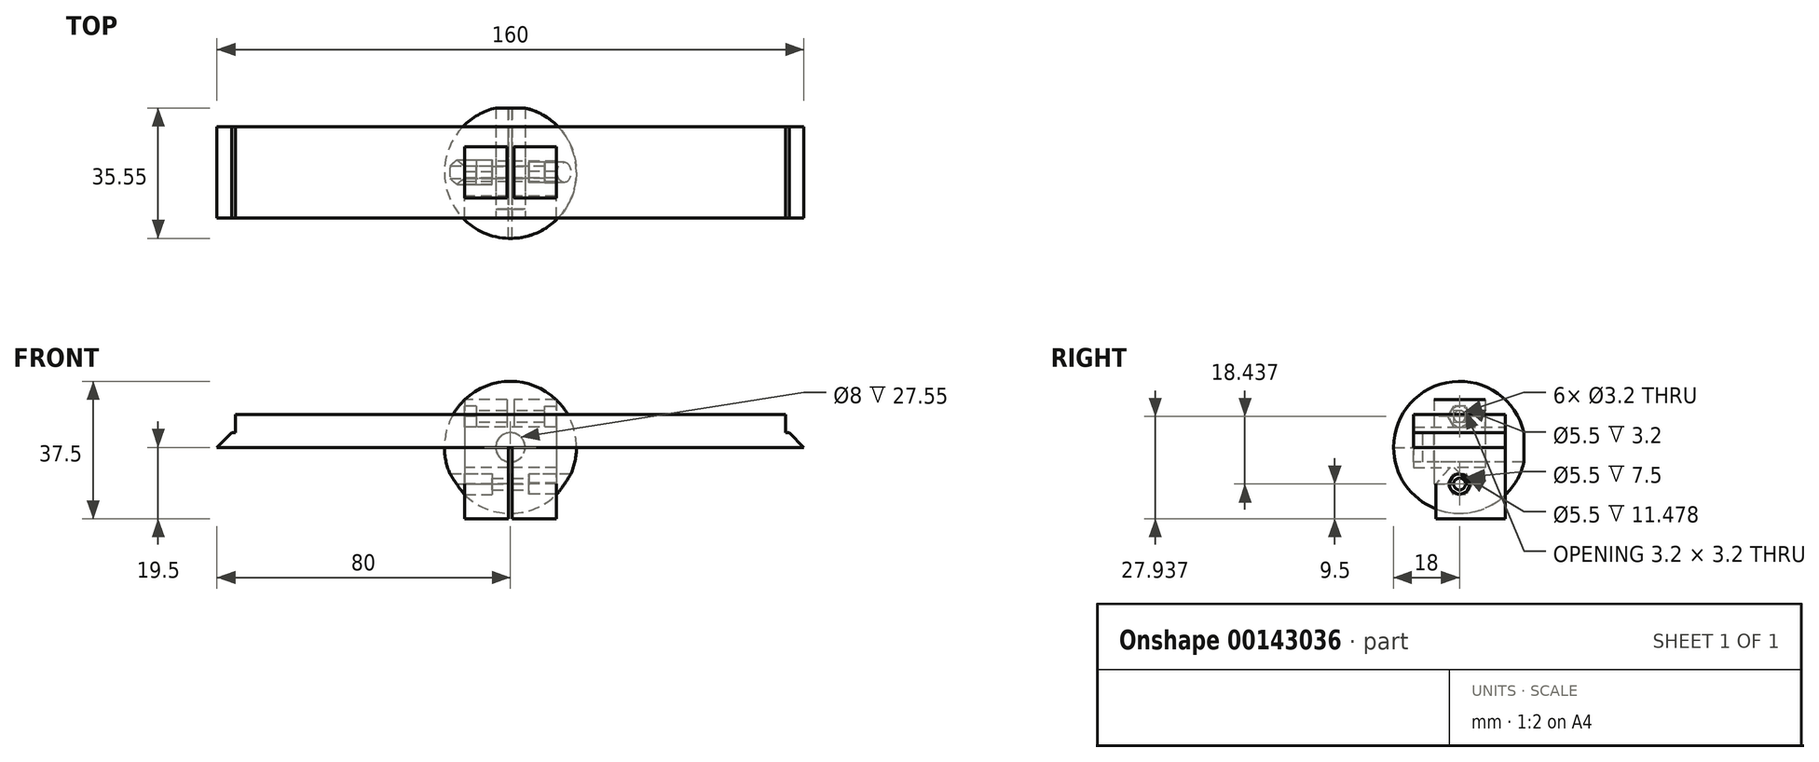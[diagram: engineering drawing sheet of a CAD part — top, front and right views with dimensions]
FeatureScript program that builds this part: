
annotation { "Feature Type Name" : "Feature", "Feature Type Description" : "" }
export const myFeature = defineFeature(function(context is Context, id is Id, definition is map)
    precondition{}
    {
        {
            var Q0;
            Q0=qCreatedBy(makeId("Right.planeOp"),FACE);
            var sketch = newSketch(context, id + "F0", { "sketchPlane" : qUnion([Q0])});
            skLineSegment(sketch, "E0.bottom", {"start": v(-7, 13) * mm, "end": v(7, 13) * mm});
            skLineSegment(sketch, "E0.top", {"start": v(-7, -10) * mm, "end": v(3, -10) * mm});
            skLineSegment(sketch, "E0.left", {"start": v(-7, 13) * mm, "end": v(-7, -10) * mm});
            skLineSegment(sketch, "E0.right", {"start": v(7, 13) * mm, "end": v(7, -5.5) * mm});
            skPoint(sketch, "E1", {"position": v(0, 13) * mm});
            skLineSegment(sketch, "E2.bottom", {"start": v(-23.43, 4) * mm, "end": v(36.95, 4) * mm, "construction": true});
            skLineSegment(sketch, "E2.top", {"start": v(-23.43, -4) * mm, "end": v(36.95, -4) * mm, "construction": true});
            skLineSegment(sketch, "E2.left", {"start": v(-23.43, 4) * mm, "end": v(-23.43, -4) * mm, "construction": true});
            skLineSegment(sketch, "E2.right", {"start": v(36.95, 4) * mm, "end": v(36.95, -4) * mm, "construction": true});
            skPoint(sketch, "E3", {"position": v(-23.43, 0) * mm});
            skLineSegment(sketch, "E4", {"start": v(7, -5.5) * mm, "end": v(-1.5, -5.5) * mm});
            skLineSegment(sketch, "E5", {"start": v(-1.5, -5.5) * mm, "end": v(3, -10) * mm});
            skSolve(sketch);
        }
        {
            var Q0;
            Q0=makeQuery(id+"F0.imprint","IMPRINT",FACE,{"disambiguationData":[TD([[makeQuery(id+"F0.imprint","IMPRINT",EDGE,{"derivedFrom":sQuery(id+"F0.wireOp",EDGE,"E0.bottom")}),-1.0]])]});
            extrude(context, id + "F1", {"entities" : qUnion([Q0]), "depth" : 25 * mm, "symmetric" : true});
        }
        {
            var Q0;
            Q0=makeQuery(id+"F1.opExtrude","SWEPT_FACE",FACE,{"disambiguationData":[OSD([sQuery(id+"F0.wireOp",EDGE,"E0.left")])]});
            var sketch = newSketch(context, id + "F2", { "sketchPlane" : qUnion([Q0])});
            skCircle(sketch, "E6", {"center": v(0, 0) * mm, "radius": 4 * mm});
            skLineSegment(sketch, "E7", {"start": v(-1, 3.87) * mm, "end": v(-1, 13) * mm});
            skLineSegment(sketch, "E8", {"start": v(-1, 13) * mm, "end": v(1, 13) * mm});
            skLineSegment(sketch, "E9", {"start": v(1, 13) * mm, "end": v(1, 3.87) * mm});
            skSolve(sketch);
        }
        {
            var Q0;
            {var subQ0=sQuery(id+"F2.wireOp",EDGE,"E7");Q0=makeQuery(id+"F2.imprint","IMPRINT",FACE,{"disambiguationData":[TD([[makeQuery(id+"F2.imprint","IMPRINT",EDGE,{"derivedFrom":subQ0}),-1.0]])]});}
            var Q1;
            {var subQ0=sQuery(id+"F2.wireOp",EDGE,"E6");var subQ1=makeQuery(id+"F2.imprint","INTERSECT",VERTEX,{"derivedFrom":[subQ0,sQuery(id+"F2.wireOp",EDGE,"E7")]});Q1=makeQuery(id+"F2.imprint","IMPRINT",FACE,{"disambiguationData":[TD([[makeQuery(id+"F2.imprint","IMPRINT",EDGE,{"disambiguationData":[TD([[subQ1,1.0]])],"derivedFrom":subQ0}),1.0]])]});}
            extrude(context, id + "F3", {"entities" : qUnion([Q0, Q1]), "operationType" : NewBodyOperationType.REMOVE, "endBound" : BoundingType.THROUGH_ALL, "oppositeDirection" : true, "depth" : 25 * mm});
        }
        {
            var Q0;
            Q0=makeQuery(id+"F1.opExtrude","CAP_FACE",FACE,{"disambiguationData":[OSD([sQuery(id+"F0.wireOp",EDGE,"E0.bottom"),sQuery(id+"F0.wireOp",EDGE,"E0.top"),sQuery(id+"F0.wireOp",EDGE,"E0.left"),sQuery(id+"F0.wireOp",EDGE,"E0.right"),sQuery(id+"F0.wireOp",EDGE,"E4"),sQuery(id+"F0.wireOp",EDGE,"E5")])],"isStart":true});
            var sketch = newSketch(context, id + "F4", { "sketchPlane" : qUnion([Q0])});
            skCircle(sketch, "E10", {"center": v(0, 8.44) * mm, "radius": 1.6 * mm});
            skPoint(sketch, "E10.centerSnap0", {"position": v(0, 13) * mm});
            skLineSegment(sketch, "E11.0", {"start": v(-7, 13) * mm, "end": v(-7, 3.87) * mm, "construction": true});
            skPoint(sketch, "E12", {"position": v(-7, 8.44) * mm});
            skSolve(sketch);
        }
        {
            var Q0;
            Q0=makeQuery(id+"F4.imprint","IMPRINT",FACE,{"disambiguationData":[TD([[makeQuery(id+"F4.imprint","IMPRINT",EDGE,{"derivedFrom":sQuery(id+"F4.wireOp",EDGE,"E10")}),1.0]])]});
            extrude(context, id + "F5", {"entities" : qUnion([Q0]), "operationType" : NewBodyOperationType.REMOVE, "endBound" : BoundingType.THROUGH_ALL, "oppositeDirection" : true, "depth" : 25 * mm});
        }
        {
            var Q0;
            Q0=makeQuery(id+"F1.opExtrude","CAP_FACE",FACE,{"disambiguationData":[OSD([sQuery(id+"F0.wireOp",EDGE,"E0.bottom"),sQuery(id+"F0.wireOp",EDGE,"E0.top"),sQuery(id+"F0.wireOp",EDGE,"E0.left"),sQuery(id+"F0.wireOp",EDGE,"E0.right"),sQuery(id+"F0.wireOp",EDGE,"E4"),sQuery(id+"F0.wireOp",EDGE,"E5")])],"isStart":true});
            var sketch = newSketch(context, id + "F6", { "sketchPlane" : qUnion([Q0])});
            skCircle(sketch, "E13.0", {"center": v(0, 8.44) * mm, "radius": 1.6 * mm, "construction": true});
            skCircle(sketch, "E14.cCircle", {"center": v(0, 8.44) * mm, "radius": 2.85 * mm, "construction": true});
            skLineSegment(sketch, "E14.0", {"start": v(1.65, 5.59) * mm, "end": v(-1.65, 5.59) * mm});
            skLineSegment(sketch, "E14.1", {"start": v(-1.65, 5.59) * mm, "end": v(-3.3, 8.44) * mm});
            skLineSegment(sketch, "E14.2", {"start": v(-3.3, 8.44) * mm, "end": v(-1.65, 11.29) * mm});
            skLineSegment(sketch, "E14.3", {"start": v(-1.65, 11.29) * mm, "end": v(1.65, 11.29) * mm});
            skLineSegment(sketch, "E14.4", {"start": v(1.65, 11.29) * mm, "end": v(3.3, 8.44) * mm});
            skLineSegment(sketch, "E14.5", {"start": v(3.3, 8.44) * mm, "end": v(1.65, 5.59) * mm});
            skPoint(sketch, "E14.0.midPoint", {"position": v(0, 5.59) * mm});
            skSolve(sketch);
        }
        {
            var Q0;
            Q0=makeQuery(id+"F6.imprint","IMPRINT",FACE,{"disambiguationData":[TD([[makeQuery(id+"F6.imprint","IMPRINT",EDGE,{"derivedFrom":sQuery(id+"F6.wireOp",EDGE,"E14.0")}),-1.0]])]});
            extrude(context, id + "F7", {"entities" : qUnion([Q0]), "operationType" : NewBodyOperationType.REMOVE, "oppositeDirection" : true, "depth" : 3.2 * mm});
        }
        {
            var Q0;
            Q0=makeQuery(id+"F1.opExtrude","CAP_FACE",FACE,{"disambiguationData":[OSD([sQuery(id+"F0.wireOp",EDGE,"E0.bottom"),sQuery(id+"F0.wireOp",EDGE,"E0.top"),sQuery(id+"F0.wireOp",EDGE,"E0.left"),sQuery(id+"F0.wireOp",EDGE,"E0.right"),sQuery(id+"F0.wireOp",EDGE,"E4"),sQuery(id+"F0.wireOp",EDGE,"E5")])],"isStart":false});
            var sketch = newSketch(context, id + "F8", { "sketchPlane" : qUnion([Q0])});
            skCircle(sketch, "E15", {"center": v(0, 8.44) * mm, "radius": 2.75 * mm});
            skSolve(sketch);
        }
        {
            var Q0;
            Q0=qSketchRegion(id+"F8",true);
            extrude(context, id + "F9", {"entities" : qUnion([Q0]), "operationType" : NewBodyOperationType.REMOVE, "oppositeDirection" : true, "depth" : 3.2 * mm});
        }
        {
            var Q0;
            Q0=qCreatedBy(makeId("Right.planeOp"),FACE);
            var sketch = newSketch(context, id + "F10", { "sketchPlane" : qUnion([Q0])});
            skLineSegment(sketch, "E16.bottom", {"start": v(-31.87, 4) * mm, "end": v(35.54, 4) * mm, "construction": true});
            skLineSegment(sketch, "E16.top", {"start": v(-31.87, -4) * mm, "end": v(35.54, -4) * mm, "construction": true});
            skLineSegment(sketch, "E16.left", {"start": v(-31.87, 4) * mm, "end": v(-31.87, -4) * mm, "construction": true});
            skLineSegment(sketch, "E16.right", {"start": v(35.54, 4) * mm, "end": v(35.54, -4) * mm, "construction": true});
            skPoint(sketch, "E17", {"position": v(-31.87, 0) * mm});
            skLineSegment(sketch, "E18.bottom", {"start": v(-12.5, 5.5) * mm, "end": v(12.5, 5.5) * mm});
            skLineSegment(sketch, "E18.top", {"start": v(-6.5, -19.5) * mm, "end": v(12.5, -19.5) * mm});
            skLineSegment(sketch, "E18.left", {"start": v(-12.5, 5.5) * mm, "end": v(-12.5, -5.5) * mm});
            skLineSegment(sketch, "E18.right", {"start": v(12.5, 5.5) * mm, "end": v(12.5, -19.5) * mm});
            skLineSegment(sketch, "E19", {"start": v(-12.5, -5.5) * mm, "end": v(-2.5, -5.5) * mm});
            skLineSegment(sketch, "E20", {"start": v(-2.5, -5.5) * mm, "end": v(-6.5, -10) * mm});
            skLineSegment(sketch, "E21", {"start": v(-6.5, -10) * mm, "end": v(-6.5, -19.5) * mm});
            skPoint(sketch, "E22", {"position": v(0, 5.5) * mm});
            skPoint(sketch, "E23", {"position": v(-12.5, 0) * mm});
            skSolve(sketch);
        }
        {
            var Q0;
            Q0=makeQuery(id+"F10.imprint","IMPRINT",FACE,{"disambiguationData":[TD([[makeQuery(id+"F10.imprint","IMPRINT",EDGE,{"derivedFrom":sQuery(id+"F10.wireOp",EDGE,"E18.bottom")}),-1.0]])]});
            extrude(context, id + "F11", {"entities" : qUnion([Q0]), "depth" : 25 * mm, "symmetric" : true});
        }
        {
            var Q0;
            Q0=makeQuery(id+"F11.opExtrude","SWEPT_FACE",FACE,{"disambiguationData":[OSD([sQuery(id+"F10.wireOp",EDGE,"E18.left")])]});
            var sketch = newSketch(context, id + "F12", { "sketchPlane" : qUnion([Q0])});
            skCircle(sketch, "E24", {"center": v(0, 0) * mm, "radius": 4 * mm});
            skSolve(sketch);
        }
        {
            var Q0;
            Q0=makeQuery(id+"F12.imprint","IMPRINT",FACE,{"disambiguationData":[TD([[makeQuery(id+"F12.imprint","IMPRINT",EDGE,{"derivedFrom":sQuery(id+"F12.wireOp",EDGE,"E24")}),1.0]])]});
            extrude(context, id + "F13", {"entities" : qUnion([Q0]), "operationType" : NewBodyOperationType.REMOVE, "endBound" : BoundingType.THROUGH_ALL, "oppositeDirection" : true, "depth" : 25 * mm});
        }
        {
            var Q0;
            Q0=qCreatedBy(makeId("Top.planeOp"),FACE);
            var sketch = newSketch(context, id + "F14", { "sketchPlane" : qUnion([Q0])});
            skArc(sketch, "E25", {"start": v(0, 18) * mm, "mid": v(-18, 0) * mm, "end": v(0, -18) * mm});
            skLineSegment(sketch, "E26", {"start": v(0, -18) * mm, "end": v(0, 18) * mm});
            skSolve(sketch);
        }
        {
            var Q0;
            Q0=makeQuery(id+"F14.imprint","IMPRINT",FACE,{"disambiguationData":[TD([[makeQuery(id+"F14.imprint","IMPRINT",EDGE,{"derivedFrom":sQuery(id+"F14.wireOp",EDGE,"E25")}),1.0]])]});
            var Q1;
            Q1=sQuery(id+"F14.wireOp",EDGE,"E26");
            revolve(context, id + "F15", {"entities" : qUnion([Q0]), "axis" : qUnion([Q1]), "revolveType" : RevolveType.FULL});
        }
        {
            var Q0;
            Q0=qCreatedBy(makeId("Front.planeOp"),FACE);
            var sketch = newSketch(context, id + "F16", { "sketchPlane" : qUnion([Q0])});
            skCircle(sketch, "E27", {"center": v(0, 0) * mm, "radius": 4 * mm});
            skSolve(sketch);
        }
        {
            var Q0;
            Q0=qSketchRegion(id+"F16",true);
            extrude(context, id + "F17", {"entities" : qUnion([Q0]), "operationType" : NewBodyOperationType.REMOVE, "oppositeDirection" : true, "depth" : 30 * mm, "hasSecondDirection" : true, "secondDirectionOppositeDirection" : false, "secondDirectionDepth" : 10 * mm});
        }
        {
            var Q0;
            Q0=qCreatedBy(makeId("Top.planeOp"),FACE);
            var sketch = newSketch(context, id + "F18", { "sketchPlane" : qUnion([Q0])});
            skLineSegment(sketch, "E28.bottom", {"start": v(-0.5, -18) * mm, "end": v(0.5, -18) * mm});
            skLineSegment(sketch, "E28.top", {"start": v(-0.5, 17.43) * mm, "end": v(0.5, 17.43) * mm});
            skLineSegment(sketch, "E28.left", {"start": v(-0.5, -18) * mm, "end": v(-0.5, 17.43) * mm});
            skLineSegment(sketch, "E28.right", {"start": v(0.5, -18) * mm, "end": v(0.5, 17.43) * mm});
            skPoint(sketch, "E29", {"position": v(0, 17.43) * mm});
            skPoint(sketch, "E30", {"position": v(0, -18) * mm});
            skArc(sketch, "E31", {"start": v(-4.5, 17.43) * mm, "mid": v(0, -18) * mm, "end": v(4.5, 17.43) * mm, "construction": true});
            skSolve(sketch);
        }
        {
            var Q0;
            Q0=makeQuery(id+"F18.imprint","IMPRINT",FACE,{"disambiguationData":[TD([[makeQuery(id+"F18.imprint","IMPRINT",EDGE,{"derivedFrom":sQuery(id+"F18.wireOp",EDGE,"E28.bottom")}),1.0]])]});
            extrude(context, id + "F19", {"entities" : qUnion([Q0]), "operationType" : NewBodyOperationType.REMOVE, "endBound" : BoundingType.THROUGH_ALL, "oppositeDirection" : true, "depth" : 25 * mm});
        }
        {
            var Q0;
            Q0=qCreatedBy(makeId("Right.planeOp"),FACE);
            var sketch = newSketch(context, id + "F20", { "sketchPlane" : qUnion([Q0])});
            skCircle(sketch, "E32", {"center": v(0, -10) * mm, "radius": 1.6 * mm});
            skSolve(sketch);
        }
        {
            var Q0;
            Q0=qSketchRegion(id+"F20",true);
            extrude(context, id + "F21", {"entities" : qUnion([Q0]), "operationType" : NewBodyOperationType.REMOVE, "oppositeDirection" : true, "depth" : 29 * mm, "symmetric" : true});
        }
        {
            var Q0;
            Q0=qCreatedBy(makeId("Right.planeOp"),FACE);
            cPlane(context, id + "F22", {"entities" : qUnion([Q0]), "cplaneType" : CPlaneType.OFFSET, "offset" : 5 * mm, "width" : 150 * mm, "height" : 150 * mm});
        }
        {
            var Q0;
            Q0=qCreatedBy(id+"F22.planeOp",FACE);
            var sketch = newSketch(context, id + "F23", { "sketchPlane" : qUnion([Q0])});
            skCircle(sketch, "E33.0", {"center": v(0, -10) * mm, "radius": 1.6 * mm, "construction": true});
            skCircle(sketch, "E34", {"center": v(0, -10) * mm, "radius": 2.75 * mm});
            skSolve(sketch);
        }
        {
            var Q0;
            Q0=qSketchRegion(id+"F23",true);
            extrude(context, id + "F24", {"entities" : qUnion([Q0]), "operationType" : NewBodyOperationType.REMOVE, "endBound" : BoundingType.THROUGH_ALL, "depth" : 25 * mm});
        }
        {
            var Q0;
            Q0=qCreatedBy(makeId("Right.planeOp"),FACE);
            cPlane(context, id + "F25", {"entities" : qUnion([Q0]), "cplaneType" : CPlaneType.OFFSET, "offset" : 5 * mm, "oppositeDirection" : true, "width" : 150 * mm, "height" : 150 * mm});
        }
        {
            var Q0;
            Q0=qCreatedBy(id+"F25.planeOp",FACE);
            var sketch = newSketch(context, id + "F26", { "sketchPlane" : qUnion([Q0])});
            skCircle(sketch, "E35.0", {"center": v(0.04, -10.02) * mm, "radius": 1.6 * mm, "construction": true});
            skCircle(sketch, "E36.cCircle", {"center": v(0.04, -10.02) * mm, "radius": 2.9 * mm, "construction": true});
            skLineSegment(sketch, "E36.0", {"start": v(1.72, -12.93) * mm, "end": v(-1.63, -12.93) * mm});
            skLineSegment(sketch, "E36.1", {"start": v(-1.63, -12.92) * mm, "end": v(-3.3, -10.02) * mm});
            skLineSegment(sketch, "E36.2", {"start": v(-3.3, -10.02) * mm, "end": v(-1.63, -7.12) * mm});
            skLineSegment(sketch, "E36.3", {"start": v(-1.63, -7.12) * mm, "end": v(1.72, -7.12) * mm});
            skLineSegment(sketch, "E36.4", {"start": v(1.72, -7.13) * mm, "end": v(3.4, -10.02) * mm});
            skLineSegment(sketch, "E36.5", {"start": v(3.4, -10.03) * mm, "end": v(1.72, -12.93) * mm});
            skPoint(sketch, "E36.0.midPoint", {"position": v(0.04, -12.93) * mm});
            skSolve(sketch);
        }
        {
            var Q0;
            Q0=qSketchRegion(id+"F26",true);
            extrude(context, id + "F27", {"entities" : qUnion([Q0]), "operationType" : NewBodyOperationType.REMOVE, "endBound" : BoundingType.THROUGH_ALL, "oppositeDirection" : true, "depth" : 25 * mm});
        }
        {
            var Q0;
            Q0=qCreatedBy(makeId("Front.planeOp"),FACE);
            var sketch = newSketch(context, id + "F28", { "sketchPlane" : qUnion([Q0])});
            skLineSegment(sketch, "E37.bottom", {"start": v(-80, 0) * mm, "end": v(80, 0) * mm});
            skLineSegment(sketch, "E37.top", {"start": v(-76, 4) * mm, "end": v(76, 4) * mm});
            skLineSegment(sketch, "E38", {"start": v(-80, 0) * mm, "end": v(-76, 4) * mm});
            skLineSegment(sketch, "E39", {"start": v(-75, 4) * mm, "end": v(-75, 9) * mm});
            skLineSegment(sketch, "E40", {"start": v(-75, 9) * mm, "end": v(75, 9) * mm});
            skLineSegment(sketch, "E41", {"start": v(75, 9) * mm, "end": v(75, 4) * mm});
            skLineSegment(sketch, "E42", {"start": v(80, 0) * mm, "end": v(76, 4) * mm});
            skPoint(sketch, "E43", {"position": v(0, 9) * mm});
            skPoint(sketch, "E44", {"position": v(0, 0) * mm});
            skSolve(sketch);
        }
        {
            var Q0;
            {var subQ0=sQuery(id+"F28.wireOp",EDGE,"E39");Q0=makeQuery(id+"F28.imprint","IMPRINT",FACE,{"disambiguationData":[TD([[makeQuery(id+"F28.imprint","IMPRINT",EDGE,{"derivedFrom":subQ0}),-1.0]])]});}
            var Q1;
            Q1=makeQuery(id+"F28.imprint","IMPRINT",FACE,{"disambiguationData":[TD([[makeQuery(id+"F28.imprint","IMPRINT",EDGE,{"derivedFrom":sQuery(id+"F28.wireOp",EDGE,"E37.bottom")}),1.0]])]});
            extrude(context, id + "F29", {"entities" : qUnion([Q0, Q1]), "depth" : 25 * mm, "symmetric" : true});
        }
    });
